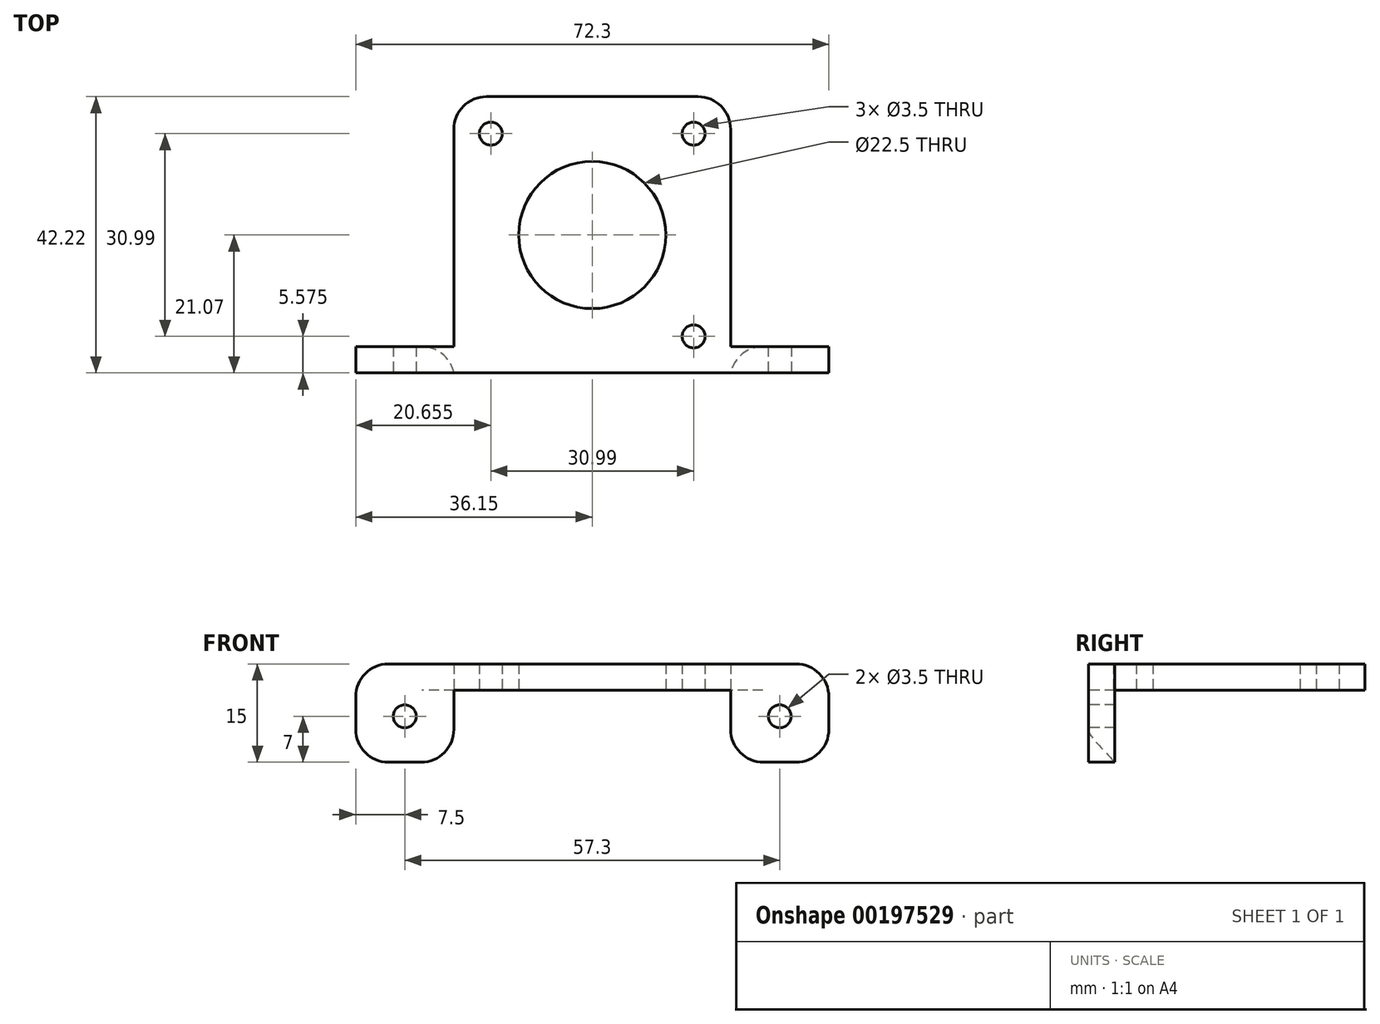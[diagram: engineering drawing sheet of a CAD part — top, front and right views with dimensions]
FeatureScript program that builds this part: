
annotation { "Feature Type Name" : "Feature", "Feature Type Description" : "" }
export const myFeature = defineFeature(function(context is Context, id is Id, definition is map)
    precondition{}
    {
        {
            var Q0;
            Q0=qCreatedBy(makeId("Top.planeOp"),FACE);
            var sketch = newSketch(context, id + "F0", { "sketchPlane" : qUnion([Q0])});
            skLineSegment(sketch, "E0.bottom", {"start": v(-21.15, 21.15) * mm, "end": v(21.15, 21.15) * mm});
            skLineSegment(sketch, "E0.left", {"start": v(-21.15, 21.15) * mm, "end": v(-21.15, -21.07) * mm});
            skLineSegment(sketch, "E0.right", {"start": v(21.15, 21.15) * mm, "end": v(21.15, -21.15) * mm});
            skLineSegment(sketch, "E1.bottom", {"start": v(-15.5, 15.5) * mm, "end": v(15.5, 15.5) * mm, "construction": true});
            skLineSegment(sketch, "E1.top", {"start": v(-15.5, -15.5) * mm, "end": v(15.5, -15.5) * mm, "construction": true});
            skLineSegment(sketch, "E1.left", {"start": v(-15.5, 15.5) * mm, "end": v(-15.5, -15.5) * mm, "construction": true});
            skLineSegment(sketch, "E1.right", {"start": v(15.5, 15.5) * mm, "end": v(15.5, -15.5) * mm, "construction": true});
            skCircle(sketch, "E2", {"center": v(-15.5, 15.5) * mm, "radius": 1.75 * mm});
            skCircle(sketch, "E3", {"center": v(-15.5, -15.5) * mm, "radius": 1.75 * mm, "construction": true});
            skCircle(sketch, "E4", {"center": v(15.5, 15.5) * mm, "radius": 1.75 * mm});
            skCircle(sketch, "E5", {"center": v(15.5, -15.5) * mm, "radius": 1.75 * mm});
            skCircle(sketch, "E6", {"center": v(0, 0) * mm, "radius": 11.25 * mm});
            skLineSegment(sketch, "E7.bottom", {"start": v(-21.15, -21.07) * mm, "end": v(21.15, -21.07) * mm});
            skLineSegment(sketch, "E7.right", {"start": v(21.15, -21.07) * mm, "end": v(21.15, -21.15) * mm});
            skSolve(sketch);
        }
        {
            var Q0;
            Q0=qSketchRegion(id+"F0",true);
            extrude(context, id + "F1", {"entities" : qUnion([Q0]), "depth" : 4 * mm});
        }
        {
            var Q0;
            Q0=makeQuery(id+"F1.opExtrude","CAP_FACE",FACE,{"disambiguationData":[OSD([sQuery(id+"F0.wireOp",EDGE,"E0.bottom"),sQuery(id+"F0.wireOp",EDGE,"E0.left"),sQuery(id+"F0.wireOp",EDGE,"E0.right"),sQuery(id+"F0.wireOp",EDGE,"E2"),sQuery(id+"F0.wireOp",EDGE,"E4"),sQuery(id+"F0.wireOp",EDGE,"E5"),sQuery(id+"F0.wireOp",EDGE,"E6"),sQuery(id+"F0.wireOp",EDGE,"E7.bottom")])],"isStart":false});
            var sketch = newSketch(context, id + "F2", { "sketchPlane" : qUnion([Q0])});
            skLineSegment(sketch, "E8.bottom", {"start": v(-21.15, -17.07) * mm, "end": v(-36.15, -17.07) * mm});
            skLineSegment(sketch, "E8.top", {"start": v(-21.15, -21.07) * mm, "end": v(-36.15, -21.07) * mm});
            skLineSegment(sketch, "E8.left", {"start": v(-21.15, -17.07) * mm, "end": v(-21.15, -21.07) * mm});
            skLineSegment(sketch, "E8.right", {"start": v(-36.15, -17.07) * mm, "end": v(-36.15, -21.07) * mm});
            skLineSegment(sketch, "E9.bottom", {"start": v(21.15, -17.07) * mm, "end": v(36.15, -17.07) * mm});
            skLineSegment(sketch, "E9.top", {"start": v(21.15, -21.07) * mm, "end": v(36.15, -21.07) * mm});
            skLineSegment(sketch, "E9.left", {"start": v(21.15, -17.07) * mm, "end": v(21.15, -21.07) * mm});
            skLineSegment(sketch, "E9.right", {"start": v(36.15, -17.07) * mm, "end": v(36.15, -21.07) * mm});
            skSolve(sketch);
        }
        {
            var Q0;
            Q0=qSketchRegion(id+"F2",true);
            extrude(context, id + "F3", {"entities" : qUnion([Q0]), "operationType" : NewBodyOperationType.ADD, "oppositeDirection" : true, "depth" : 15 * mm});
        }
        {
            var Q0;
            Q0=makeQuery(id+"F1.opExtrude","SWEPT_EDGE",EDGE,{"disambiguationData":[OSD([sQuery(id+"F0.wireOp",EDGE,"E0.bottom"),sQuery(id+"F0.wireOp",EDGE,"E0.right")])]});
            var Q1;
            Q1=makeQuery(id+"F1.opExtrude","SWEPT_EDGE",EDGE,{"disambiguationData":[OSD([sQuery(id+"F0.wireOp",EDGE,"E0.bottom"),sQuery(id+"F0.wireOp",EDGE,"E0.left")])]});
            var Q2;
            {var subQ0=sQuery(id+"F2.wireOp",EDGE,"E8.bottom");var subQ1=sQuery(id+"F0.wireOp",EDGE,"E0.left");var subQ9=sQuery(id+"F2.wireOp",EDGE,"E8.left");Q2=makeQuery(id+"F3.boolean.opBoolean","SPLIT",EDGE,{"disambiguationData":[TD([makeQuery(id+"F3.opExtrude","CAP_FACE",FACE,{"disambiguationData":[OSD([subQ0,sQuery(id+"F2.wireOp",EDGE,"E8.top"),subQ9,sQuery(id+"F2.wireOp",EDGE,"E8.right")])],"isStart":true})])],"derivedFrom":makeQuery(id+"F3.opExtrude","SWEPT_EDGE",EDGE,{"disambiguationData":[OSD([subQ1,subQ0,subQ9])]})});}
            var Q3;
            {var subQ5=sQuery(id+"F0.wireOp",EDGE,"E0.right");var subQ8=sQuery(id+"F2.wireOp",EDGE,"E9.left");var subQ9=sQuery(id+"F2.wireOp",EDGE,"E9.bottom");Q3=makeQuery(id+"F3.boolean.opBoolean","SPLIT",EDGE,{"disambiguationData":[TD([makeQuery(id+"F3.opExtrude","CAP_FACE",FACE,{"disambiguationData":[OSD([sQuery(id+"F2.wireOp",EDGE,"E8.bottom"),sQuery(id+"F2.wireOp",EDGE,"E8.top"),sQuery(id+"F2.wireOp",EDGE,"E8.left"),sQuery(id+"F2.wireOp",EDGE,"E8.right")])],"isStart":true})])],"derivedFrom":makeQuery(id+"F3.opExtrude","SWEPT_EDGE",EDGE,{"disambiguationData":[OSD([subQ5,subQ9,subQ8])]})});}
            var Q4;
            Q4=makeQuery(id+"F3.opExtrude","CAP_EDGE",EDGE,{"disambiguationData":[OSD([sQuery(id+"F2.wireOp",EDGE,"E9.right")])],"isStart":true});
            var Q5;
            Q5=makeQuery(id+"F3.opExtrude","CAP_EDGE",EDGE,{"disambiguationData":[OSD([sQuery(id+"F2.wireOp",EDGE,"E8.right")])],"isStart":true});
            var Q6;
            Q6=makeQuery(id+"F3.opExtrude","CAP_EDGE",EDGE,{"disambiguationData":[OSD([sQuery(id+"F2.wireOp",EDGE,"E9.right")])],"isStart":false});
            var Q7;
            Q7=makeQuery(id+"F3.opExtrude","CAP_EDGE",EDGE,{"disambiguationData":[OSD([sQuery(id+"F2.wireOp",EDGE,"E9.left")])],"isStart":false});
            var Q8;
            Q8=makeQuery(id+"F3.opExtrude","CAP_EDGE",EDGE,{"disambiguationData":[OSD([sQuery(id+"F2.wireOp",EDGE,"E8.left")])],"isStart":false});
            var Q9;
            Q9=makeQuery(id+"F3.opExtrude","CAP_EDGE",EDGE,{"disambiguationData":[OSD([sQuery(id+"F2.wireOp",EDGE,"E8.right")])],"isStart":false});
            fillet(context, id + "F4", {"entities" : qUnion([Q0, Q1, Q2, Q3, Q4, Q5, Q6, Q7, Q8, Q9]), "radius" : 5 * mm, "tangentPropagation" : true, "allowEdgeOverflow" : false});
        }
        {
            var Q0;
            Q0=makeQuery(id+"F3.boolean.opBoolean","MERGE",FACE,{"derivedFrom":[makeQuery(id+"F1.opExtrude","SWEPT_FACE",FACE,{"disambiguationData":[OSD([sQuery(id+"F0.wireOp",EDGE,"E7.bottom")])]}),makeQuery(id+"F3.opExtrude","SWEPT_FACE",FACE,{"disambiguationData":[OSD([sQuery(id+"F2.wireOp",EDGE,"E8.top")])]}),makeQuery(id+"F3.opExtrude","SWEPT_FACE",FACE,{"disambiguationData":[OSD([sQuery(id+"F2.wireOp",EDGE,"E9.top")])]})]});
            var sketch = newSketch(context, id + "F5", { "sketchPlane" : qUnion([Q0])});
            skCircle(sketch, "E10", {"center": v(-28.65, -4) * mm, "radius": 1.75 * mm});
            skCircle(sketch, "E11", {"center": v(28.65, -4) * mm, "radius": 1.75 * mm});
            skSolve(sketch);
        }
        {
            var Q0;
            Q0=qSketchRegion(id+"F5",true);
            extrude(context, id + "F6", {"entities" : qUnion([Q0]), "operationType" : NewBodyOperationType.REMOVE, "endBound" : BoundingType.UP_TO_NEXT, "oppositeDirection" : true, "depth" : 25 * mm});
        }
    });
